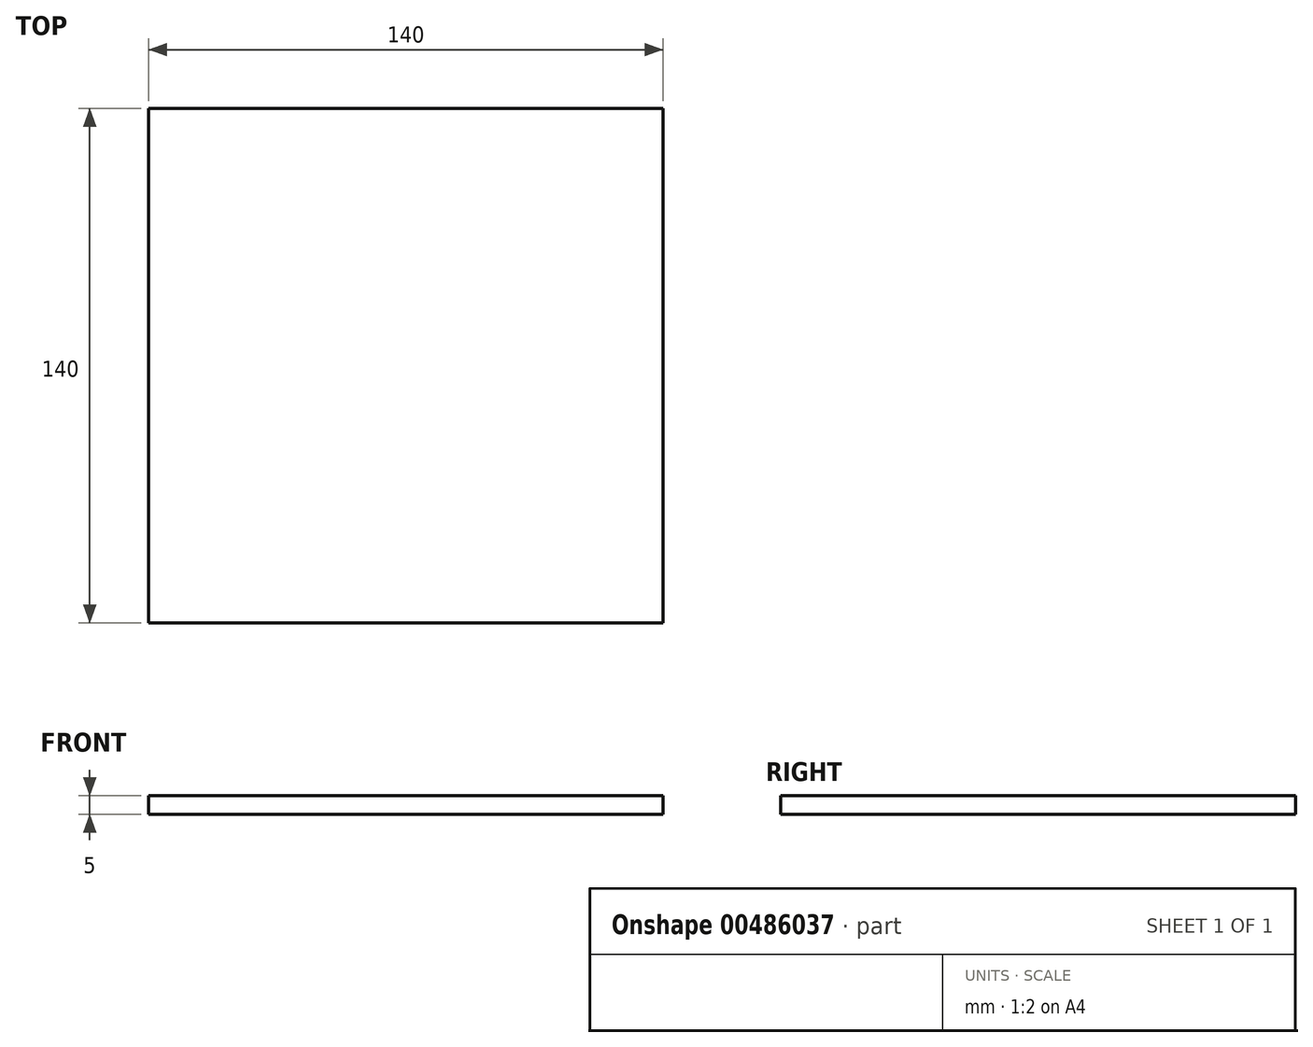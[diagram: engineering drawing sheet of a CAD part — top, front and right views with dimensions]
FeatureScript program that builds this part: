
annotation { "Feature Type Name" : "Feature", "Feature Type Description" : "" }
export const myFeature = defineFeature(function(context is Context, id is Id, definition is map)
    precondition{}
    {
        {
            var Q0;
            Q0=qCreatedBy(makeId("Top.planeOp"),FACE);
            var sketch = newSketch(context, id + "F0", { "sketchPlane" : qUnion([Q0])});
            skLineSegment(sketch, "E0.bottom", {"start": v(70, 70) * mm, "end": v(-70, 70) * mm});
            skLineSegment(sketch, "E0.top", {"start": v(70, -70) * mm, "end": v(-70, -70) * mm});
            skLineSegment(sketch, "E0.left", {"start": v(70, 70) * mm, "end": v(70, -70) * mm});
            skLineSegment(sketch, "E0.right", {"start": v(-70, 70) * mm, "end": v(-70, -70) * mm});
            skPoint(sketch, "E0.middle", {"position": v(0, 0) * mm});
            skSolve(sketch);
        }
        {
            var Q0;
            Q0=makeQuery(id+"F0.imprint","IMPRINT",FACE,{"disambiguationData":[TD([[makeQuery(id+"F0.imprint","IMPRINT",EDGE,{"derivedFrom":sQuery(id+"F0.wireOp",EDGE,"E0.bottom")}),1.0]])]});
            extrude(context, id + "F1", {"entities" : qUnion([Q0]), "depth" : 5 * mm});
        }
    });
